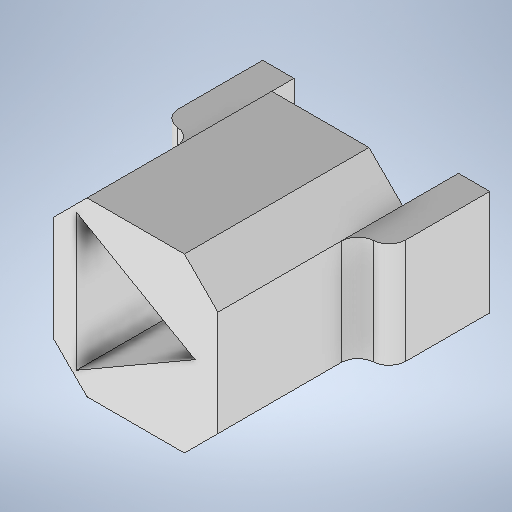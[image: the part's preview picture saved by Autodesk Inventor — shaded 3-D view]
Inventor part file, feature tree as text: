
AUTODESK INVENTOR PART (.ipt)
format: ipt  version: 2025.1 (Build 291241000, 241)  size: 275,456 bytes
history: native  units: mm
features: extrude x5, sketch x3, chamfer x1, fillet x1, projected_geometry x1
ambient origin geometry x8: Origin, YZ Plane, XZ Plane, XY Plane, X Axis, Y Axis, Z Axis, Center Point
bodies: Solid1 (feature_tree)
feature tree (11):
  sketch  "Sketch1"  dims[d0=29.4mm d1=18.8mm]
  extrude  "Extrusion1"  Depth=18.8mm
  extrude  "Extrusion2"  Depth=14.7mm
  sketch  "Sketch2"  dims[d2=9.4mm d3=14.7mm]
  extrude  "Extrusion3"  Depth=5.6mm
  extrude  "Extrusion4"  Depth=18.0mm TaperAngle=0.0deg
  chamfer  "Chamfer1"  Distance=10.0mm
  fillet  "Fillet1"  Radius=21.2mm
  extrude  "Extrusion5"  TaperAngle=0.0deg  [1 undecoded]
  sketch  "Sketch4"  dims[d4=5.6mm d5=5.6mm d6=18.0mm d7=0.0mm d8=10.0mm d9=0.0mm d17=21.2mm d18=0.0mm d19=21.2mm d20=21.2mm d21=10.6mm d25=6.0mm d26=6.0mm d27=0.0mm d28=0.0mm d29=10.0mm d30=8.0mm d31=0.0mm d32=0.0mm d33=8.0mm d34=0.0mm d35=6.0mm d36=2.0mm d37=45.0deg d38=3.0mm d39=15.0mm d40=0.0mm]
  projected_geometry  "Projected Loop1"
note: 1 required parameter value undecoded (feature->parameter linkage not recoverable at this tier; creation-order binding heuristic only, values carry confidence <= 0.55)
